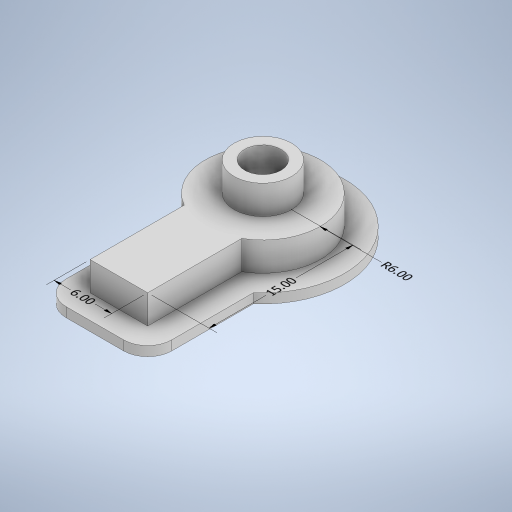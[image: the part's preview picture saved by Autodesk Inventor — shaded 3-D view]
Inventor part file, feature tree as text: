
AUTODESK INVENTOR PART (.ipt)
format: ipt  version: 2024.1 (Build 281209000, 209)  size: 321,024 bytes
history: native  units: mm
features: extrude x5, sketch x5, other x4, fillet x1, projected_geometry x1
ambient origin geometry x8: Origin, YZ Plane, XZ Plane, XY Plane, X Axis, Y Axis, Z Axis, Center Point
bodies: Body1 (feature_tree)
feature tree (16):
  other  "ソリッド1"
  extrude  "押し出し1"  Depth=12.0mm
  extrude  "押し出し2"  Depth=1.0mm TaperAngle=0.0deg
  extrude  "押し出し3"  Depth=6.0mm
  extrude  "押し出し4"  Depth=3.0mm TaperAngle=0.0deg
  extrude  "押し出し5"  Depth=3.8mm
  fillet  "フィレット1"  [1 undecoded]
  sketch  "スケッチ1"
  sketch  "スケッチ2"
  sketch  "スケッチ3"
  sketch  "スケッチ5"
  projected_geometry  "投影ループ1"
  sketch  "スケッチ6"
  other  "半径寸法 1"
  other  "長さ寸法 1"
  other  "長さ寸法 2"
note: 1 required parameter value undecoded (feature->parameter linkage not recoverable at this tier; creation-order binding heuristic only, values carry confidence <= 0.55)
